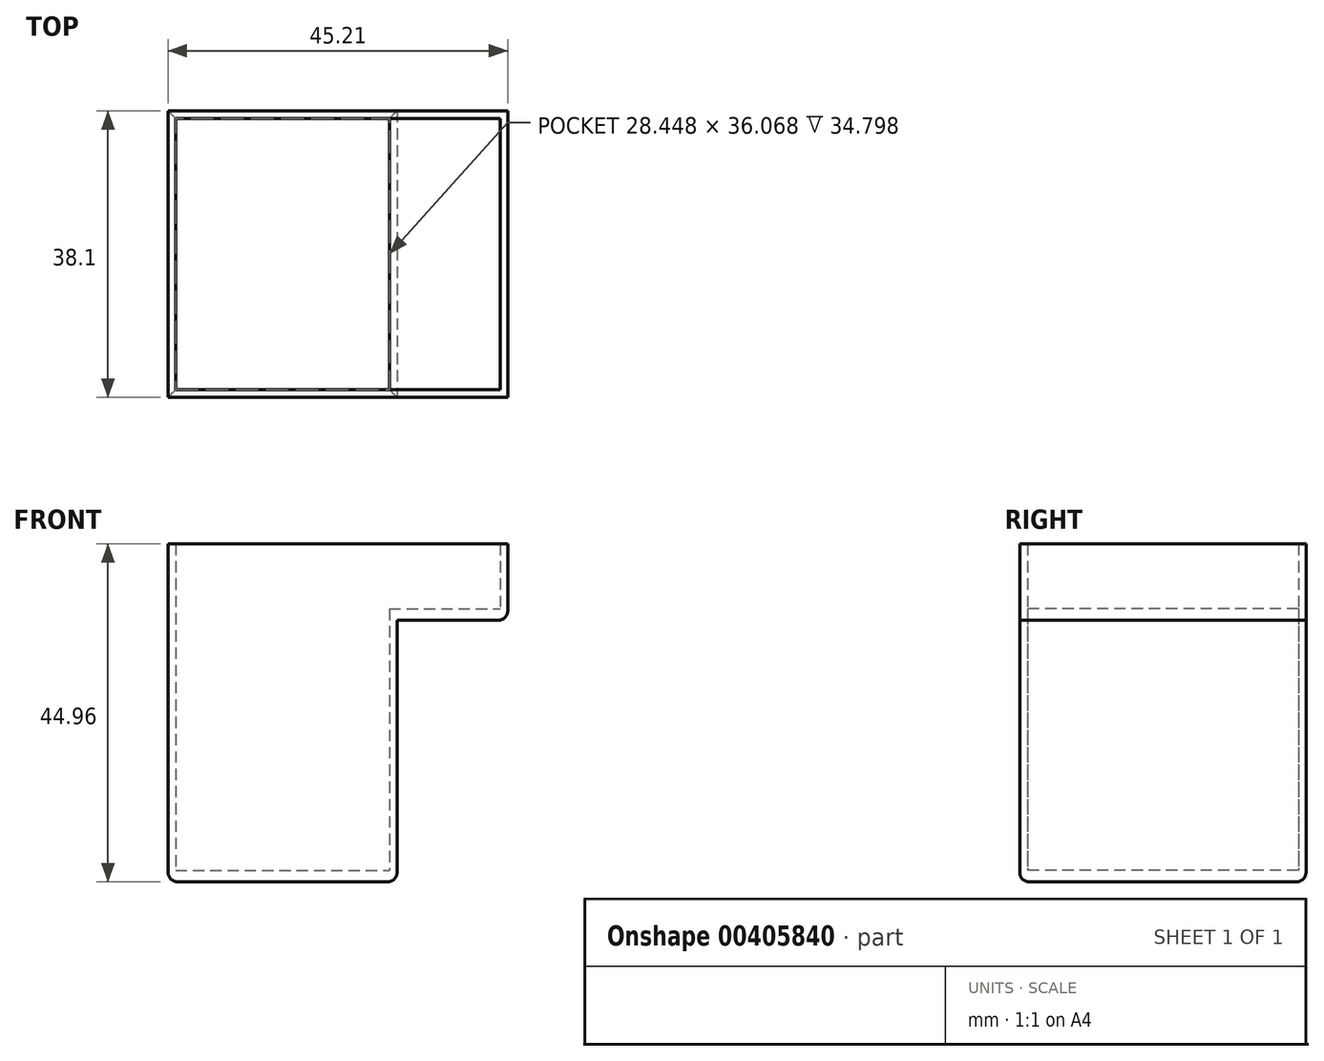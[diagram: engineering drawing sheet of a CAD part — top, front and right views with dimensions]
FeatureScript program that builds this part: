
annotation { "Feature Type Name" : "Feature", "Feature Type Description" : "" }
export const myFeature = defineFeature(function(context is Context, id is Id, definition is map)
    precondition{}
    {
        {
            var Q0;
            Q0=qCreatedBy(makeId("Top.planeOp"),FACE);
            var sketch = newSketch(context, id + "F0", { "sketchPlane" : qUnion([Q0])});
            skLineSegment(sketch, "E0.bottom", {"start": v(-15.24, 19.05) * mm, "end": v(15.24, 19.05) * mm});
            skLineSegment(sketch, "E0.top", {"start": v(-15.24, -19.05) * mm, "end": v(15.24, -19.05) * mm});
            skLineSegment(sketch, "E0.left", {"start": v(-15.24, 19.05) * mm, "end": v(-15.24, -19.05) * mm});
            skLineSegment(sketch, "E0.right", {"start": v(15.24, 19.05) * mm, "end": v(15.24, -19.05) * mm});
            skPoint(sketch, "E0.middle", {"position": v(0, 0) * mm});
            skSolve(sketch);
        }
        {
            var Q0;
            Q0=qSketchRegion(id+"F0",true);
            extrude(context, id + "F1", {"entities" : qUnion([Q0]), "depth" : 1.52 * mm});
        }
        {
            var Q0;
            Q0=makeQuery(id+"F1.opExtrude","CAP_FACE",FACE,{"disambiguationData":[OSD([sQuery(id+"F0.wireOp",EDGE,"E0.bottom"),sQuery(id+"F0.wireOp",EDGE,"E0.top"),sQuery(id+"F0.wireOp",EDGE,"E0.left"),sQuery(id+"F0.wireOp",EDGE,"E0.right")])],"isStart":false});
            var sketch = newSketch(context, id + "F2", { "sketchPlane" : qUnion([Q0])});
            skLineSegment(sketch, "E1.bottom", {"start": v(-14.22, 18.03) * mm, "end": v(14.22, 18.03) * mm});
            skLineSegment(sketch, "E1.top", {"start": v(-14.22, -18.03) * mm, "end": v(14.22, -18.03) * mm});
            skLineSegment(sketch, "E1.left", {"start": v(-14.22, 18.03) * mm, "end": v(-14.22, -18.03) * mm});
            skLineSegment(sketch, "E1.right", {"start": v(14.22, 18.03) * mm, "end": v(14.22, -18.03) * mm});
            skPoint(sketch, "E1.middle", {"position": v(0, 0) * mm});
            skSolve(sketch);
        }
        {
            var Q0;
            Q0=makeQuery(id+"F2.imprint","IMPRINT",FACE,{"disambiguationData":[TD([[makeQuery(id+"F2.imprint","IMPRINT",EDGE,{"derivedFrom":sQuery(id+"F2.wireOp",EDGE,"E1.bottom")}),1.0]])]});
            extrude(context, id + "F3", {"entities" : qUnion([Q0]), "operationType" : NewBodyOperationType.ADD, "depth" : 33.27 * mm});
        }
        {
            var Q0;
            Q0=makeQuery(id+"F1.opExtrude","CAP_FACE",FACE,{"disambiguationData":[OSD([sQuery(id+"F0.wireOp",EDGE,"E0.bottom"),sQuery(id+"F0.wireOp",EDGE,"E0.top"),sQuery(id+"F0.wireOp",EDGE,"E0.left"),sQuery(id+"F0.wireOp",EDGE,"E0.right")])],"isStart":true});
            fillet(context, id + "F4", {"entities" : qUnion([Q0]), "radius" : 1.27 * mm, "tangentPropagation" : true, "allowEdgeOverflow" : false});
        }
        {
            var Q0;
            Q0=makeQuery(id+"F3.opExtrude","CAP_FACE",FACE,{"disambiguationData":[OSD([sQuery(id+"F0.wireOp",EDGE,"E0.bottom"),sQuery(id+"F0.wireOp",EDGE,"E0.top"),sQuery(id+"F0.wireOp",EDGE,"E0.left"),sQuery(id+"F0.wireOp",EDGE,"E0.right"),sQuery(id+"F2.wireOp",EDGE,"E1.bottom"),sQuery(id+"F2.wireOp",EDGE,"E1.top"),sQuery(id+"F2.wireOp",EDGE,"E1.left"),sQuery(id+"F2.wireOp",EDGE,"E1.right")])],"isStart":false});
            var sketch = newSketch(context, id + "F5", { "sketchPlane" : qUnion([Q0])});
            skLineSegment(sketch, "E2", {"start": v(-15.24, 19.05) * mm, "end": v(29.97, 19.05) * mm});
            skLineSegment(sketch, "E3.MirrorCS", {"start": v(-15.24, -19.05) * mm, "end": v(29.97, -19.05) * mm});
            skLineSegment(sketch, "E4", {"start": v(-15.24, 19.05) * mm, "end": v(-15.24, -19.05) * mm});
            skLineSegment(sketch, "E5", {"start": v(29.97, 19.05) * mm, "end": v(29.97, -19.05) * mm});
            skLineSegment(sketch, "E6.bottom", {"start": v(14.22, -18.03) * mm, "end": v(-14.22, -18.03) * mm});
            skLineSegment(sketch, "E6.top", {"start": v(14.22, 18.03) * mm, "end": v(-14.22, 18.03) * mm});
            skLineSegment(sketch, "E6.left", {"start": v(14.22, -18.03) * mm, "end": v(14.22, 18.03) * mm});
            skLineSegment(sketch, "E6.right", {"start": v(-14.22, -18.03) * mm, "end": v(-14.22, 18.03) * mm});
            skPoint(sketch, "E6.middle", {"position": v(0, 0) * mm});
            skSolve(sketch);
        }
        {
            var Q0;
            Q0 = qSketchRegion(id + "F5", true);
            extrude(context, id + "F6", {"entities" : qUnion([Q0]), "operationType" : NewBodyOperationType.ADD, "depth" : 1.52 * mm});
        }
        {
            var Q0;
            Q0=makeQuery(id+"F6.opExtrude","CAP_FACE",FACE,{"disambiguationData":[OSD([sQuery(id+"F5.wireOp",EDGE,"E2"),sQuery(id+"F5.wireOp",EDGE,"E3.MirrorCS"),sQuery(id+"F5.wireOp",EDGE,"E4"),sQuery(id+"F5.wireOp",EDGE,"E5"),sQuery(id+"F5.wireOp",EDGE,"E6.bottom"),sQuery(id+"F5.wireOp",EDGE,"E6.top"),sQuery(id+"F5.wireOp",EDGE,"E6.left"),sQuery(id+"F5.wireOp",EDGE,"E6.right")])],"isStart":false});
            var sketch = newSketch(context, id + "F7", { "sketchPlane" : qUnion([Q0])});
            skLineSegment(sketch, "E7", {"start": v(-15.24, 19.05) * mm, "end": v(29.97, 19.05) * mm});
            skLineSegment(sketch, "E8.MirrorCS", {"start": v(-15.24, -19.05) * mm, "end": v(29.97, -19.05) * mm});
            skLineSegment(sketch, "E9", {"start": v(-15.24, 19.05) * mm, "end": v(-15.24, -19.05) * mm});
            skLineSegment(sketch, "E10", {"start": v(29.97, 19.05) * mm, "end": v(29.97, -19.05) * mm});
            skPoint(sketch, "E11.middle", {"position": v(0, 0) * mm});
            skLineSegment(sketch, "E12.0", {"start": v(-14.22, 18.03) * mm, "end": v(-14.22, -18.03) * mm});
            skLineSegment(sketch, "E12.1", {"start": v(-14.22, 18.03) * mm, "end": v(28.96, 18.03) * mm});
            skLineSegment(sketch, "E12.2", {"start": v(28.96, 18.03) * mm, "end": v(28.96, -18.03) * mm});
            skLineSegment(sketch, "E12.3", {"start": v(-14.22, -18.03) * mm, "end": v(28.96, -18.03) * mm});
            skSolve(sketch);
        }
        {
            var Q0;
            Q0 = qSketchRegion(id + "F7", true);
            extrude(context, id + "F8", {"entities" : qUnion([Q0]), "operationType" : NewBodyOperationType.ADD, "depth" : 8.64 * mm});
        }
        {
            var Q0;
            Q0=makeQuery(id+"F6.opExtrude","CAP_EDGE",EDGE,{"disambiguationData":[OSD([sQuery(id+"F5.wireOp",EDGE,"E5")])],"isStart":true});
            fillet(context, id + "F9", {"entities" : qUnion([Q0]), "radius" : 1.27 * mm, "tangentPropagation" : true, "allowEdgeOverflow" : false});
        }
    });
